# Revit family: Shutter-Wood-Fypon-Board_Batten-Quarter_Round
name_source: partatom
category: Specialty Equipment
units: mm (PartAtom-declared; Revit-internal decimal feet)

## family parameters
Classification Number = 23.30.60.11.14
Cut with Voids When Loaded = No
Enable Cutting in Views = No
Host = Face
Maintain Annotation Orientation = No
Part Type = Normal
Room Calculation Point = No
Round Connector Dimension = Use Diameter
Shared = No

## types (1)
- default load type catalog
    2 Batten = Yes
    2 Board = No
    3 Board = No
    3rd Board = Yes
    4 Board = Yes
    Assembly Code = B20
    Board Depth = 0' - 1 1/2"
    Board Width = 0' - 6"
    Bottom Batten Offset = 0' - 5 19/32"
    Default Elevation = 4' - 0"
    Description = Rough Sawn Quarter Round Cedar Shutters
    Finish = Wood-Fypon-Rough_Sawn
    Height = 6' - 0"
    Manufacturer = Fypon
    Model = default loat type catalog
    Product Documentation Link = http://www.fypon.com
    Product Name = Board and Batten Shutter
    Product Page URL = http://www.fypon.com
    Specification = http://www.fypon.com
    Top Batten Offset = 2' - 0"
    Type Comments = default load type catalog
    URL = http://www.fypon.com
    Width = 2' - 0"

## geometry (parser evidence)
native form markers: Sweep x2
no freeform markers — native parametric forms only
